# Revit family: BC_URMET_BA-OF-90_LOD400_
name_source: partatom
category: Dispositifs de sécurité
revit_build: Autodesk Revit 2017 (Build: 20160225_1515(x64)
units: mm (PartAtom-declared; Revit-internal decimal feet)

## family parameters
Conserver l'orientation des annotations = Non
Cote de connecteur circulaire = Utiliser le diamètre
Couper avec des vides une fois chargée = Non
Hôte = Face
Numéro OmniClass = 23.85.30.11
Partagée = Non
Point de calcul de pièce = Non
Titre OmniClass = Access Controls
Type d'élément = Normal

## types (2) — shared parameters
Couleur = Urmet-BAOF90LH
Elévation par défaut = 1219 mm
Fabricant = Urmet
Largeur Hors Tout = 96 mm  [stored 0.314961 ft]
Longueur Hors Tout = 95 mm  [stored 0.31168 ft]
Modèle = BA/OF/90LH

## per-type parameters (varying)
| type | Embase | Epaisseur Hors Tout | Hauteur bouton |
| BA/OF/90LH - Embase | Oui | 39 mm  [stored 0.127953 ft] | 0 mm  [stored 0 ft] |
| BA/OF/90LH | Non | 24 mm  [stored 0.0787402 ft] | 15 mm  [stored 0.0492126 ft] |

note: column(s) folded — value = type name in every type: Commentaires du type

note: [stored X ft] marks values corroborated as IEEE doubles in the binary element streams (Revit-internal decimal feet)
